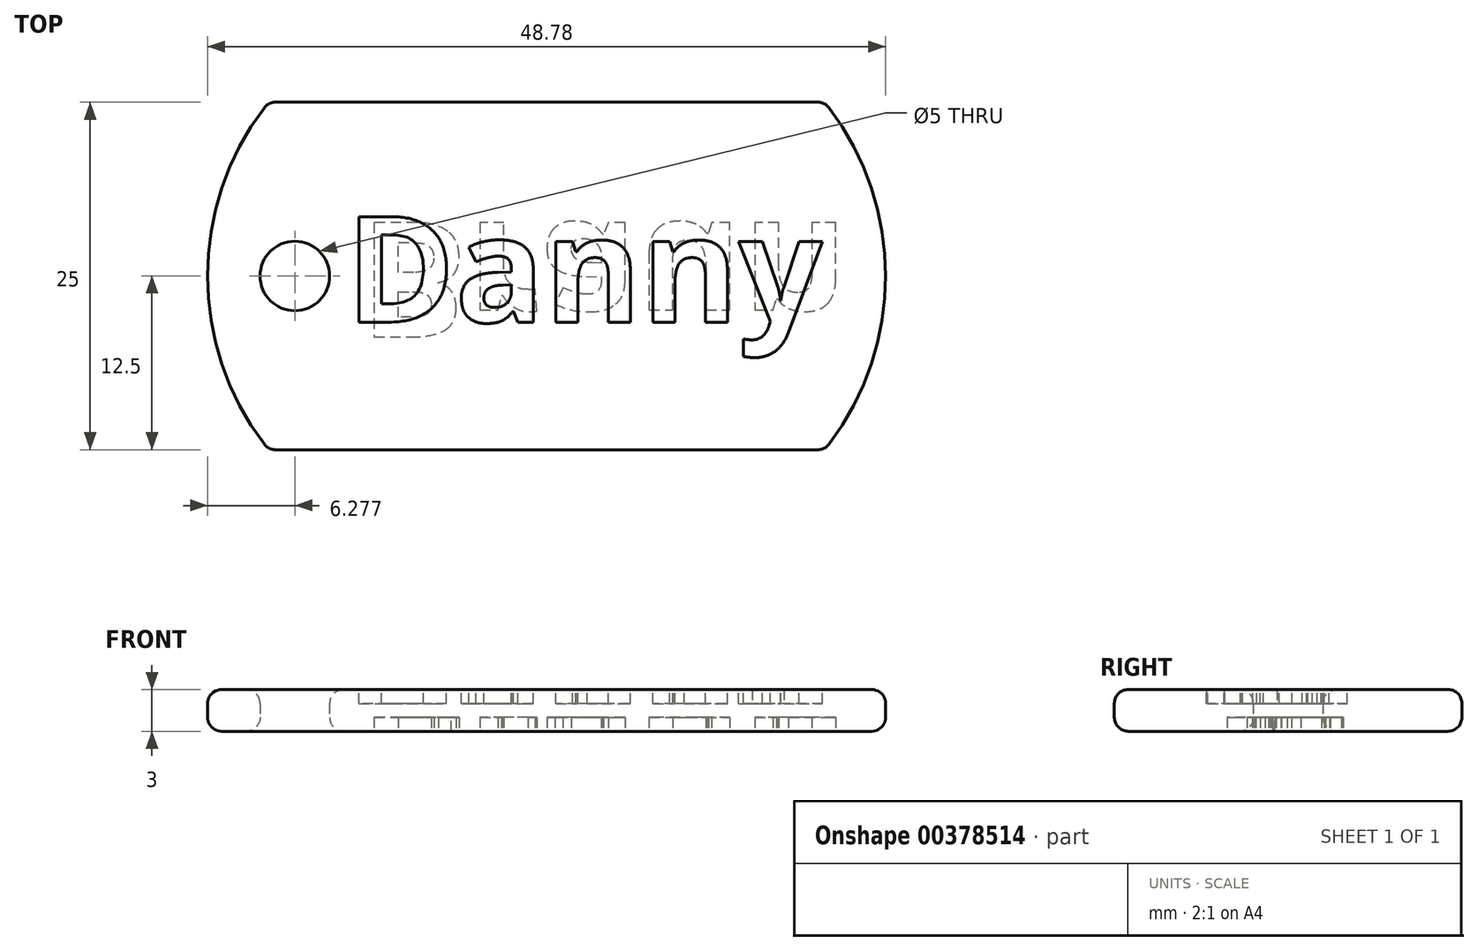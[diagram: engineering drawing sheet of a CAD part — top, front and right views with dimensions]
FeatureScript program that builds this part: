
annotation { "Feature Type Name" : "Feature", "Feature Type Description" : "" }
export const myFeature = defineFeature(function(context is Context, id is Id, definition is map)
    precondition{}
    {
        {
            var Q0;
            Q0=qCreatedBy(makeId("Top.planeOp"),FACE);
            var sketch = newSketch(context, id + "F0", { "sketchPlane" : qUnion([Q0])});
            skLineSegment(sketch, "E0.bottom", {"start": v(-20, 12.5) * mm, "end": v(20, 12.5) * mm});
            skLineSegment(sketch, "E0.top", {"start": v(-20, -12.5) * mm, "end": v(20, -12.5) * mm});
            skArc(sketch, "E1", {"start": v(-20, 12.5) * mm, "mid": v(-24.39, 0) * mm, "end": v(-20, -12.5) * mm});
            skArc(sketch, "E2", {"start": v(20, -12.5) * mm, "mid": v(24.39, 0) * mm, "end": v(20, 12.5) * mm});
            skCircle(sketch, "E3", {"center": v(-18.11, 0) * mm, "radius": 2.5 * mm});
            skSolve(sketch);
        }
        {
            var Q0;
            Q0=makeQuery(id+"F0.imprint","IMPRINT",FACE,{"disambiguationData":[TD([[makeQuery(id+"F0.imprint","IMPRINT",EDGE,{"derivedFrom":sQuery(id+"F0.wireOp",EDGE,"E0.bottom")}),-1.0]])]});
            extrude(context, id + "F1", {"entities" : qUnion([Q0]), "depth" : 3 * mm});
        }
        {
            var Q0;
            Q0=makeQuery(id+"F1.opExtrude","CAP_FACE",FACE,{"disambiguationData":[OSD([sQuery(id+"F0.wireOp",EDGE,"E0.bottom"),sQuery(id+"F0.wireOp",EDGE,"E0.top"),sQuery(id+"F0.wireOp",EDGE,"E1"),sQuery(id+"F0.wireOp",EDGE,"E2"),sQuery(id+"F0.wireOp",EDGE,"E3")])],"isStart":false});
            var sketch = newSketch(context, id + "F2", { "sketchPlane" : qUnion([Q0])});
            skText(sketch, "E4", { "text": "Danny", "fontName": "OpenSans-Bold.ttf"});
            const initialGuessF2  = {"E4": [-0.01445, -0.00332, 1, 0, 0.00765]};
            skSetInitialGuess(sketch, initialGuessF2);
            skSolve(sketch);
        }
        {
            var Q0;
            Q0=qSketchRegion(id+"F2",true);
            extrude(context, id + "F3", {"entities" : qUnion([Q0]), "operationType" : NewBodyOperationType.REMOVE, "oppositeDirection" : true, "depth" : 1 * mm});
        }
        {
            var Q0;
            Q0=makeQuery(id+"F1.opExtrude","CAP_FACE",FACE,{"disambiguationData":[OSD([sQuery(id+"F0.wireOp",EDGE,"E0.bottom"),sQuery(id+"F0.wireOp",EDGE,"E0.top"),sQuery(id+"F0.wireOp",EDGE,"E1"),sQuery(id+"F0.wireOp",EDGE,"E2"),sQuery(id+"F0.wireOp",EDGE,"E3")])],"isStart":true});
            var sketch = newSketch(context, id + "F4", { "sketchPlane" : qUnion([Q0])});
            skText(sketch, "E5", { "text": "Braun", "fontName": "OpenSans-Bold.ttf"});
            const initialGuessF4  = {"E5": [-0.01344, -0.00384, 1, 0, 0.0083]};
            skSetInitialGuess(sketch, initialGuessF4);
            skSolve(sketch);
        }
        {
            var Q0;
            Q0=qSketchRegion(id+"F4",true);
            extrude(context, id + "F5", {"entities" : qUnion([Q0]), "operationType" : NewBodyOperationType.REMOVE, "oppositeDirection" : true, "depth" : 1 * mm});
        }
        {
            var Q0;
            Q0=makeQuery(id+"F1.opExtrude","SWEPT_FACE",FACE,{"disambiguationData":[OSD([sQuery(id+"F0.wireOp",EDGE,"E2")])]});
            var Q1;
            Q1=makeQuery(id+"F1.opExtrude","SWEPT_FACE",FACE,{"disambiguationData":[OSD([sQuery(id+"F0.wireOp",EDGE,"E0.top")])]});
            var Q2;
            Q2=makeQuery(id+"F1.opExtrude","SWEPT_FACE",FACE,{"disambiguationData":[OSD([sQuery(id+"F0.wireOp",EDGE,"E3")])]});
            var Q3;
            Q3=makeQuery(id+"F1.opExtrude","SWEPT_FACE",FACE,{"disambiguationData":[OSD([sQuery(id+"F0.wireOp",EDGE,"E1")])]});
            var Q4;
            Q4=makeQuery(id+"F1.opExtrude","SWEPT_FACE",FACE,{"disambiguationData":[OSD([sQuery(id+"F0.wireOp",EDGE,"E0.bottom")])]});
            fillet(context, id + "F6", {"entities" : qUnion([Q0, Q1, Q2, Q3, Q4]), "radius" : 1 * mm, "tangentPropagation" : true, "allowEdgeOverflow" : false});
        }
    });
